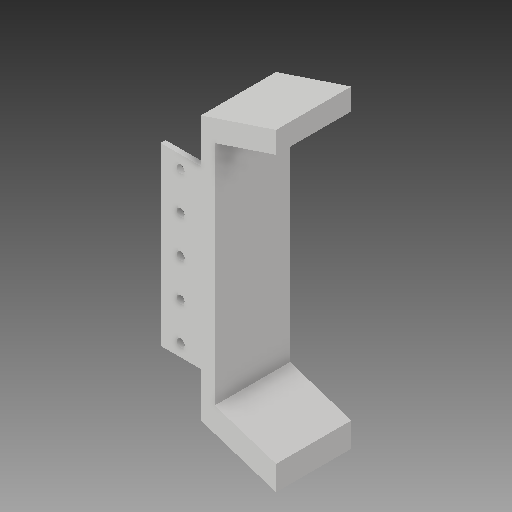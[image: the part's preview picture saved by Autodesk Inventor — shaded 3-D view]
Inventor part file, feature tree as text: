
AUTODESK INVENTOR PART (.ipt)
format: ipt  version: 2019 (Build 230136000, 136)  size: 129,536 bytes
history: native  units: mm
features: sketch x4, extrude x3, other x1, hole x1
ambient origin geometry x8: Origin, YZ Plane, XZ Plane, XY Plane, X Axis, Y Axis, Z Axis, Center Point
bodies: Body1 (feature_tree)
feature tree (9):
  other  "Sólido1"
  extrude  "Extrusión1"  Depth=70.0mm
  extrude  "Extrusión2"  Depth=30.0mm
  extrude  "Extrusión3"  Depth=30.0mm TaperAngle=0.0deg
  hole  "Agujero1"  [1 undecoded]
  sketch  "Boceto1"  dims[d0=16.0mm d1=70.0mm]
  sketch  "Boceto2"  dims[d2=2.0mm d3=0.0mm d4=30.0mm]
  sketch  "Boceto3"  dims[d5=125.0mm d6=30.0mm d7=0.0mm]
  sketch  "Boceto4"  dims[d8=0.0mm d9=0.0mm d10=3.175mm d11=6.0mm d12=4.0mm d13=2.0mm d14=90.0deg d15=8.0mm d16=20.594885mm]
note: 1 required parameter value undecoded (feature->parameter linkage not recoverable at this tier; creation-order binding heuristic only, values carry confidence <= 0.55)
